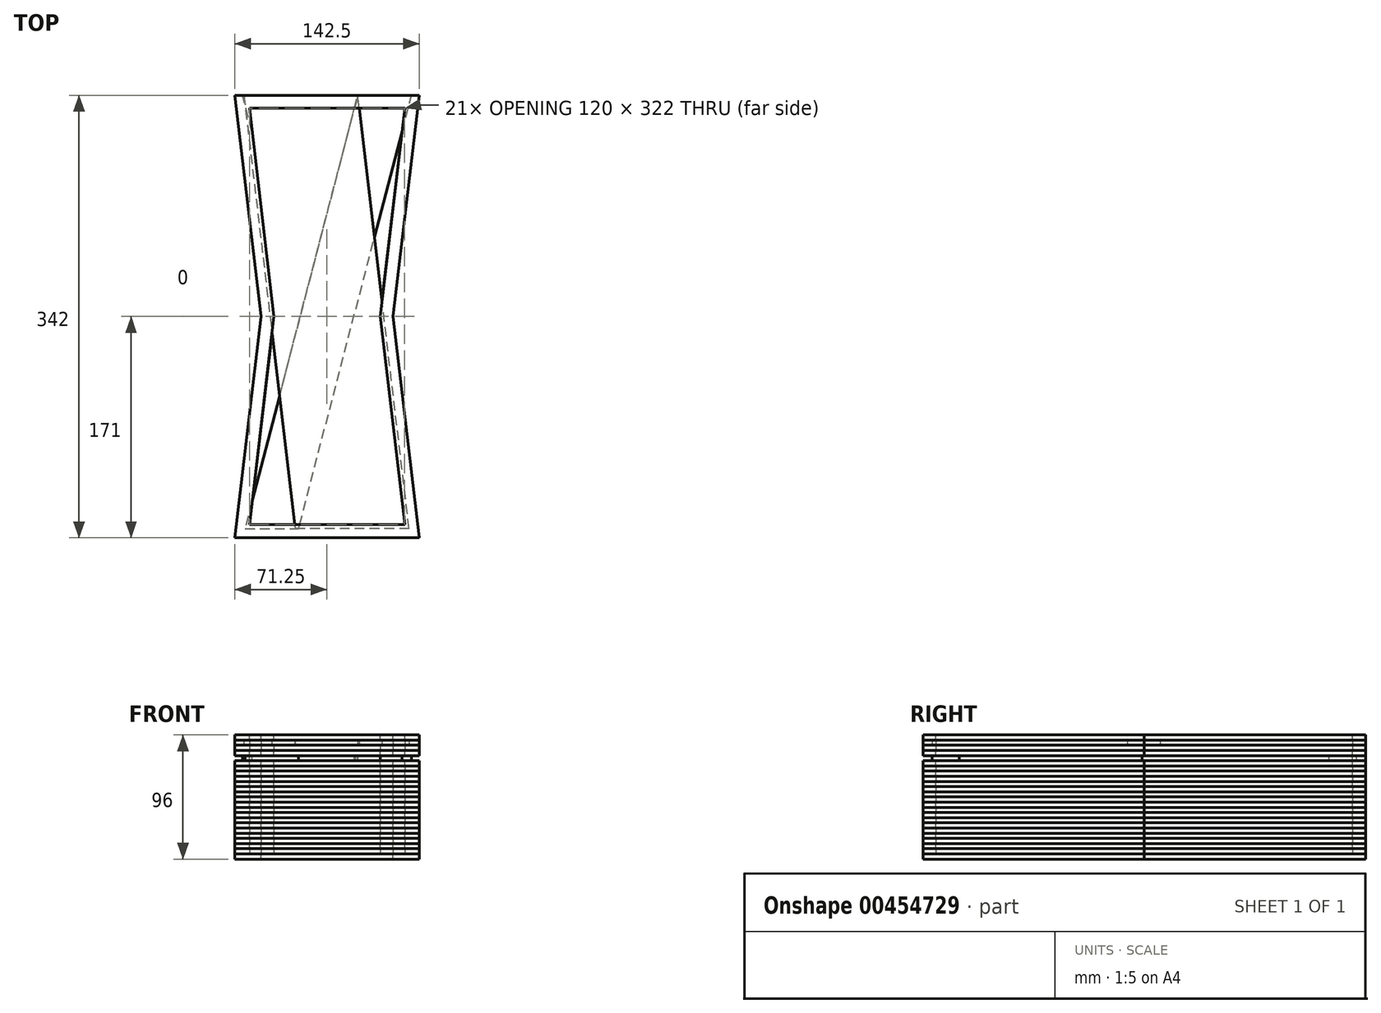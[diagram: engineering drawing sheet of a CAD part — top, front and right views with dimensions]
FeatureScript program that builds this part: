
annotation { "Feature Type Name" : "Feature", "Feature Type Description" : "" }
export const myFeature = defineFeature(function(context is Context, id is Id, definition is map)
    precondition{}
    {
        {
            var Q0;
            Q0=qCreatedBy(makeId("Top.planeOp"),FACE);
            var sketch = newSketch(context, id + "F0", { "sketchPlane" : qUnion([Q0])});
            skLineSegment(sketch, "E0", {"start": v(-71.25, -171) * mm, "end": v(-51.07, 0) * mm});
            skLineSegment(sketch, "E1", {"start": v(-51.07, 0) * mm, "end": v(-71.25, 171) * mm});
            skLineSegment(sketch, "E2", {"start": v(-71.25, 171) * mm, "end": v(71.25, 171) * mm});
            skLineSegment(sketch, "E3", {"start": v(71.25, 171) * mm, "end": v(51.07, 0) * mm});
            skLineSegment(sketch, "E4", {"start": v(51.07, 0) * mm, "end": v(71.25, -171) * mm});
            skLineSegment(sketch, "E5", {"start": v(71.25, -171) * mm, "end": v(-71.25, -171) * mm});
            skLineSegment(sketch, "E6", {"start": v(-60, -161) * mm, "end": v(-41, 0) * mm});
            skLineSegment(sketch, "E7", {"start": v(-41, 0) * mm, "end": v(-60, 161) * mm});
            skLineSegment(sketch, "E8", {"start": v(-60, 161) * mm, "end": v(60, 161) * mm});
            skLineSegment(sketch, "E9", {"start": v(60, 161) * mm, "end": v(41, 0) * mm});
            skLineSegment(sketch, "E10", {"start": v(41, 0) * mm, "end": v(60, -161) * mm});
            skLineSegment(sketch, "E11", {"start": v(60, -161) * mm, "end": v(-60, -161) * mm});
            skSolve(sketch);
        }
        {
            var Q0;
            Q0 = qSketchRegion(id + "F0", true);
            extrude(context, id + "F1", {"entities" : qUnion([Q0]), "depth" : 4 * mm});
        }
        {
            var Q0;
            Q0=makeQuery(id+"F1.opExtrude","CAP_FACE",FACE,{"disambiguationData":[OSD([sQuery(id+"F0.wireOp",EDGE,"E0"),sQuery(id+"F0.wireOp",EDGE,"E1"),sQuery(id+"F0.wireOp",EDGE,"E2"),sQuery(id+"F0.wireOp",EDGE,"E3"),sQuery(id+"F0.wireOp",EDGE,"E4"),sQuery(id+"F0.wireOp",EDGE,"E5"),sQuery(id+"F0.wireOp",EDGE,"E6"),sQuery(id+"F0.wireOp",EDGE,"E7"),sQuery(id+"F0.wireOp",EDGE,"E8"),sQuery(id+"F0.wireOp",EDGE,"E9"),sQuery(id+"F0.wireOp",EDGE,"E10"),sQuery(id+"F0.wireOp",EDGE,"E11")])],"isStart":false});
            var sketch = newSketch(context, id + "F2", { "sketchPlane" : qUnion([Q0])});
            skLineSegment(sketch, "E12", {"start": v(-71.25, -171) * mm, "end": v(-51.07, 0) * mm});
            skLineSegment(sketch, "E13", {"start": v(-51.07, 0) * mm, "end": v(-71.25, 171) * mm});
            skLineSegment(sketch, "E14", {"start": v(-71.25, 171) * mm, "end": v(-64.2, 171) * mm});
            skLineSegment(sketch, "E15", {"start": v(71.25, 171) * mm, "end": v(51.07, 0) * mm});
            skLineSegment(sketch, "E16", {"start": v(51.07, 0) * mm, "end": v(71.25, -171) * mm});
            skLineSegment(sketch, "E17", {"start": v(71.25, -171) * mm, "end": v(-71.25, -171) * mm});
            skLineSegment(sketch, "E18", {"start": v(63.38, -164) * mm, "end": v(42.46, 12.4) * mm});
            skLineSegment(sketch, "E19", {"start": v(42.46, 12.4) * mm, "end": v(60, 161) * mm});
            skLineSegment(sketch, "E20", {"start": v(60, 161) * mm, "end": v(24.84, 161) * mm});
            skLineSegment(sketch, "E21", {"start": v(24.84, 161) * mm, "end": v(24.49, 164) * mm});
            skLineSegment(sketch, "E22", {"start": v(-63.37, 164) * mm, "end": v(-42.52, -12.89) * mm});
            skLineSegment(sketch, "E23", {"start": v(-42.52, -12.89) * mm, "end": v(-60, -161) * mm});
            skLineSegment(sketch, "E24", {"start": v(-60, -161) * mm, "end": v(-25.06, -161) * mm});
            skLineSegment(sketch, "E25", {"start": v(-25.06, -161) * mm, "end": v(-24.7, -164) * mm});
            skLineSegment(sketch, "E26", {"start": v(63.38, -164) * mm, "end": v(-24.7, -164) * mm});
            skLineSegment(sketch, "E27", {"start": v(-63.37, 164) * mm, "end": v(-64.2, 171) * mm});
            skLineSegment(sketch, "E28", {"start": v(24.49, 164) * mm, "end": v(23.66, 171) * mm});
            skLineSegment(sketch, "E29.trimOffspring", {"start": v(23.66, 171) * mm, "end": v(71.25, 171) * mm});
            skSolve(sketch);
        }
        {
            var Q0;
            Q0 = qSketchRegion(id + "F2", true);
            extrude(context, id + "F3", {"entities" : qUnion([Q0]), "depth" : 4 * mm});
        }
        {
            var Q0;
            Q0=makeQuery(id+"F1.opExtrude","CAP_FACE",FACE,{"disambiguationData":[OSD([sQuery(id+"F0.wireOp",EDGE,"E0"),sQuery(id+"F0.wireOp",EDGE,"E1"),sQuery(id+"F0.wireOp",EDGE,"E2"),sQuery(id+"F0.wireOp",EDGE,"E3"),sQuery(id+"F0.wireOp",EDGE,"E4"),sQuery(id+"F0.wireOp",EDGE,"E5"),sQuery(id+"F0.wireOp",EDGE,"E6"),sQuery(id+"F0.wireOp",EDGE,"E7"),sQuery(id+"F0.wireOp",EDGE,"E8"),sQuery(id+"F0.wireOp",EDGE,"E9"),sQuery(id+"F0.wireOp",EDGE,"E10"),sQuery(id+"F0.wireOp",EDGE,"E11")])],"isStart":false});
            var Q1;
            Q1=makeQuery(id+"F3.opExtrude","CAP_FACE",FACE,{"disambiguationData":[OSD([sQuery(id+"F2.wireOp",EDGE,"E12"),sQuery(id+"F2.wireOp",EDGE,"E13"),sQuery(id+"F2.wireOp",EDGE,"E14"),sQuery(id+"F2.wireOp",EDGE,"E15"),sQuery(id+"F2.wireOp",EDGE,"E16"),sQuery(id+"F2.wireOp",EDGE,"E17"),sQuery(id+"F2.wireOp",EDGE,"E18"),sQuery(id+"F2.wireOp",EDGE,"E19"),sQuery(id+"F2.wireOp",EDGE,"E20"),sQuery(id+"F2.wireOp",EDGE,"E21"),sQuery(id+"F2.wireOp",EDGE,"E22"),sQuery(id+"F2.wireOp",EDGE,"E23"),sQuery(id+"F2.wireOp",EDGE,"E24"),sQuery(id+"F2.wireOp",EDGE,"E25"),sQuery(id+"F2.wireOp",EDGE,"E26"),sQuery(id+"F2.wireOp",EDGE,"E27"),sQuery(id+"F2.wireOp",EDGE,"E28"),sQuery(id+"F2.wireOp",EDGE,"E29.trimOffspring")])],"isStart":false});
            cPlane(context, id + "F4", {"entities" : qUnion([Q0, Q1]), "cplaneType" : CPlaneType.MID_PLANE, "offset" : 25 * mm, "width" : 150 * mm, "height" : 150 * mm});
        }
        {
            var Q0;
            Q0=makeQuery(id+"F1.opExtrude","SWEPT_BODY",BODY,{"disambiguationData":[OSD([sQuery(id+"F0.wireOp",EDGE,"E0"),sQuery(id+"F0.wireOp",EDGE,"E1"),sQuery(id+"F0.wireOp",EDGE,"E2"),sQuery(id+"F0.wireOp",EDGE,"E3"),sQuery(id+"F0.wireOp",EDGE,"E4"),sQuery(id+"F0.wireOp",EDGE,"E5"),sQuery(id+"F0.wireOp",EDGE,"E6"),sQuery(id+"F0.wireOp",EDGE,"E7"),sQuery(id+"F0.wireOp",EDGE,"E8"),sQuery(id+"F0.wireOp",EDGE,"E9"),sQuery(id+"F0.wireOp",EDGE,"E10"),sQuery(id+"F0.wireOp",EDGE,"E11")])]});
            var Q1;
            Q1=qCreatedBy(id+"F4.planeOp",FACE);
            mirror(context, id + "F5", {"entities" : qUnion([Q0]), "mirrorPlane" : qUnion([Q1])});
        }
        {
            var Q0;
            Q0=makeQuery(id+"F1.opExtrude","CAP_FACE",FACE,{"disambiguationData":[OSD([sQuery(id+"F0.wireOp",EDGE,"E0"),sQuery(id+"F0.wireOp",EDGE,"E1"),sQuery(id+"F0.wireOp",EDGE,"E2"),sQuery(id+"F0.wireOp",EDGE,"E3"),sQuery(id+"F0.wireOp",EDGE,"E4"),sQuery(id+"F0.wireOp",EDGE,"E5"),sQuery(id+"F0.wireOp",EDGE,"E6"),sQuery(id+"F0.wireOp",EDGE,"E7"),sQuery(id+"F0.wireOp",EDGE,"E8"),sQuery(id+"F0.wireOp",EDGE,"E9"),sQuery(id+"F0.wireOp",EDGE,"E10"),sQuery(id+"F0.wireOp",EDGE,"E11")])],"isStart":false});
            var sketch = newSketch(context, id + "F6", { "sketchPlane" : qUnion([Q0])});
            skLineSegment(sketch, "E30", {"start": v(-64.24, 171) * mm, "end": v(-24.7, -164) * mm});
            skLineSegment(sketch, "E31", {"start": v(23.66, 171) * mm, "end": v(-64.24, 171) * mm});
            skLineSegment(sketch, "E32", {"start": v(-24.7, -164) * mm, "end": v(63.38, -164) * mm});
            skLineSegment(sketch, "E33", {"start": v(63.38, -164) * mm, "end": v(23.66, 171) * mm});
            skSolve(sketch);
        }
        {
            var Q0;
            Q0 = qSketchRegion(id + "F6", true);
            extrude(context, id + "F7", {"entities" : qUnion([Q0]), "depth" : 4 * mm});
        }
        {
            var Q0;
            Q0=makeQuery(id+"F1.opExtrude","SWEPT_BODY",BODY,{"disambiguationData":[OSD([sQuery(id+"F0.wireOp",EDGE,"E0"),sQuery(id+"F0.wireOp",EDGE,"E1"),sQuery(id+"F0.wireOp",EDGE,"E2"),sQuery(id+"F0.wireOp",EDGE,"E3"),sQuery(id+"F0.wireOp",EDGE,"E4"),sQuery(id+"F0.wireOp",EDGE,"E5"),sQuery(id+"F0.wireOp",EDGE,"E6"),sQuery(id+"F0.wireOp",EDGE,"E7"),sQuery(id+"F0.wireOp",EDGE,"E8"),sQuery(id+"F0.wireOp",EDGE,"E9"),sQuery(id+"F0.wireOp",EDGE,"E10"),sQuery(id+"F0.wireOp",EDGE,"E11")])]});
            var Q1;
            Q1=makeQuery(id+"F1.opExtrude","CAP_FACE",FACE,{"disambiguationData":[OSD([sQuery(id+"F0.wireOp",EDGE,"E0"),sQuery(id+"F0.wireOp",EDGE,"E1"),sQuery(id+"F0.wireOp",EDGE,"E2"),sQuery(id+"F0.wireOp",EDGE,"E3"),sQuery(id+"F0.wireOp",EDGE,"E4"),sQuery(id+"F0.wireOp",EDGE,"E5"),sQuery(id+"F0.wireOp",EDGE,"E6"),sQuery(id+"F0.wireOp",EDGE,"E7"),sQuery(id+"F0.wireOp",EDGE,"E8"),sQuery(id+"F0.wireOp",EDGE,"E9"),sQuery(id+"F0.wireOp",EDGE,"E10"),sQuery(id+"F0.wireOp",EDGE,"E11")])],"isStart":true});
            mirror(context, id + "F8", {"entities" : qUnion([Q0]), "mirrorPlane" : qUnion([Q1])});
        }
        {
            var Q0;
            Q0=makeQuery(id+"F8.opPattern","COPY",FACE,{"derivedFrom":makeQuery(id+"F1.opExtrude","CAP_FACE",FACE,{"disambiguationData":[OSD([sQuery(id+"F0.wireOp",EDGE,"E0"),sQuery(id+"F0.wireOp",EDGE,"E1"),sQuery(id+"F0.wireOp",EDGE,"E2"),sQuery(id+"F0.wireOp",EDGE,"E3"),sQuery(id+"F0.wireOp",EDGE,"E4"),sQuery(id+"F0.wireOp",EDGE,"E5"),sQuery(id+"F0.wireOp",EDGE,"E6"),sQuery(id+"F0.wireOp",EDGE,"E7"),sQuery(id+"F0.wireOp",EDGE,"E8"),sQuery(id+"F0.wireOp",EDGE,"E9"),sQuery(id+"F0.wireOp",EDGE,"E10"),sQuery(id+"F0.wireOp",EDGE,"E11")])],"isStart":false}),"instanceName":"1"});
            var sketch = newSketch(context, id + "F9", { "sketchPlane" : qUnion([Q0])});
            skLineSegment(sketch, "E34", {"start": v(-71.25, -171) * mm, "end": v(-51.07, 0) * mm});
            skLineSegment(sketch, "E35", {"start": v(-51.07, 0) * mm, "end": v(-71.25, 171) * mm});
            skLineSegment(sketch, "E36", {"start": v(-71.25, 171) * mm, "end": v(71.25, 171) * mm});
            skLineSegment(sketch, "E37", {"start": v(71.25, 171) * mm, "end": v(51.07, 0) * mm});
            skLineSegment(sketch, "E38", {"start": v(51.07, 0) * mm, "end": v(71.25, -171) * mm});
            skLineSegment(sketch, "E39", {"start": v(71.25, -171) * mm, "end": v(-23.82, -171) * mm});
            skLineSegment(sketch, "E40", {"start": v(41, 0) * mm, "end": v(57.89, 143.12) * mm});
            skLineSegment(sketch, "E41", {"start": v(57.89, 143.12) * mm, "end": v(63.32, 164) * mm});
            skLineSegment(sketch, "E42", {"start": v(63.32, 164) * mm, "end": v(21.96, 164) * mm});
            skLineSegment(sketch, "E43", {"start": v(21.96, 164) * mm, "end": v(21.18, 161) * mm});
            skLineSegment(sketch, "E44", {"start": v(21.18, 161) * mm, "end": v(-60, 161) * mm});
            skLineSegment(sketch, "E45", {"start": v(-60, 161) * mm, "end": v(-41, 0) * mm});
            skLineSegment(sketch, "E46", {"start": v(-41, 0) * mm, "end": v(-57.85, -142.75) * mm});
            skLineSegment(sketch, "E47", {"start": v(-57.85, -142.75) * mm, "end": v(-63.37, -164) * mm});
            skLineSegment(sketch, "E48", {"start": v(-22, -164) * mm, "end": v(-21.22, -161) * mm});
            skLineSegment(sketch, "E49", {"start": v(-21.22, -161) * mm, "end": v(60, -161) * mm});
            skLineSegment(sketch, "E50", {"start": v(60, -161) * mm, "end": v(41, 0) * mm});
            skLineSegment(sketch, "E51", {"start": v(-63.37, -164) * mm, "end": v(-65.2, -171) * mm});
            skLineSegment(sketch, "E52", {"start": v(-22, -164) * mm, "end": v(-23.82, -171) * mm});
            skLineSegment(sketch, "E53.trimOffspring", {"start": v(-65.2, -171) * mm, "end": v(-71.25, -171) * mm});
            skLineSegment(sketch, "E54", {"start": v(0, 0) * mm, "end": v(0, -54.2) * mm, "construction": true});
            skLineSegment(sketch, "E55.MirrorCS", {"start": v(22, -164) * mm, "end": v(21.22, -161) * mm});
            skLineSegment(sketch, "E56.MirrorCS", {"start": v(22, -164) * mm, "end": v(23.82, -171) * mm});
            skLineSegment(sketch, "E57.MirrorCS", {"start": v(65.2, -171) * mm, "end": v(71.25, -171) * mm});
            skLineSegment(sketch, "E58.MirrorCS", {"start": v(63.37, -164) * mm, "end": v(65.2, -171) * mm});
            skLineSegment(sketch, "E59.MirrorCS", {"start": v(-21.96, 164) * mm, "end": v(-21.18, 161) * mm});
            skLineSegment(sketch, "E60.MirrorCS", {"start": v(51.07, 0) * mm, "end": v(71.25, 171) * mm});
            skLineSegment(sketch, "E61.MirrorCS", {"start": v(21.22, -161) * mm, "end": v(-60, -161) * mm});
            skLineSegment(sketch, "E62.MirrorCS", {"start": v(-57.89, 143.12) * mm, "end": v(-63.32, 164) * mm});
            skLineSegment(sketch, "E63.MirrorCS", {"start": v(71.25, -171) * mm, "end": v(51.07, 0) * mm});
            skLineSegment(sketch, "E64.MirrorCS", {"start": v(-60, -161) * mm, "end": v(-41, 0) * mm});
            skLineSegment(sketch, "E65.MirrorCS", {"start": v(71.25, 171) * mm, "end": v(-71.25, 171) * mm});
            skLineSegment(sketch, "E66.MirrorCS", {"start": v(60, 161) * mm, "end": v(41, 0) * mm});
            skLineSegment(sketch, "E67.MirrorCS", {"start": v(-63.32, 164) * mm, "end": v(-21.96, 164) * mm});
            skLineSegment(sketch, "E68.MirrorCS", {"start": v(57.85, -142.75) * mm, "end": v(63.37, -164) * mm});
            skLineSegment(sketch, "E69.MirrorCS", {"start": v(41, 0) * mm, "end": v(57.85, -142.75) * mm});
            skLineSegment(sketch, "E70.MirrorCS", {"start": v(-21.18, 161) * mm, "end": v(60, 161) * mm});
            skLineSegment(sketch, "E71.MirrorCS", {"start": v(-71.25, -171) * mm, "end": v(23.82, -171) * mm});
            skLineSegment(sketch, "E72.MirrorCS", {"start": v(-41, 0) * mm, "end": v(-57.89, 143.12) * mm});
            skLineSegment(sketch, "E73.MirrorCS", {"start": v(-71.25, 171) * mm, "end": v(-51.07, 0) * mm});
            skLineSegment(sketch, "E74.MirrorCS", {"start": v(-51.07, 0) * mm, "end": v(-71.25, -171) * mm});
            skSolve(sketch);
        }
        {
            var Q0;
            {var subQ8=sQuery(id+"F9.wireOp",EDGE,"E41");Q0=makeQuery(id+"F9.imprint","IMPRINT",FACE,{"disambiguationData":[TD([[makeQuery(id+"F9.imprint","IMPRINT",EDGE,{"derivedFrom":subQ8}),-1.0]])]});}
            var sketch = newSketch(context, id + "F10", { "sketchPlane" : qUnion([Q0])});
            skLineSegment(sketch, "E75", {"start": v(71.25, -171) * mm, "end": v(51.07, 0) * mm});
            skLineSegment(sketch, "E76", {"start": v(51.07, 0) * mm, "end": v(71.25, 171) * mm});
            skLineSegment(sketch, "E77", {"start": v(71.25, 171) * mm, "end": v(-71.25, 171) * mm});
            skLineSegment(sketch, "E78", {"start": v(-71.25, 171) * mm, "end": v(-51.07, 0) * mm});
            skLineSegment(sketch, "E79", {"start": v(-51.07, 0) * mm, "end": v(-71.25, -171) * mm});
            skLineSegment(sketch, "E80", {"start": v(-71.25, -171) * mm, "end": v(71.25, -171) * mm});
            skLineSegment(sketch, "E81", {"start": v(-41, 0) * mm, "end": v(-57.89, 143.12) * mm});
            skLineSegment(sketch, "E82", {"start": v(-57.89, 143.12) * mm, "end": v(-63.32, 164) * mm});
            skLineSegment(sketch, "E83", {"start": v(-63.32, 164) * mm, "end": v(-21.96, 164) * mm});
            skLineSegment(sketch, "E84", {"start": v(-21.96, 164) * mm, "end": v(-21.18, 161) * mm});
            skLineSegment(sketch, "E85", {"start": v(-21.18, 161) * mm, "end": v(60, 161) * mm});
            skLineSegment(sketch, "E86", {"start": v(60, 161) * mm, "end": v(41, 0) * mm});
            skLineSegment(sketch, "E87", {"start": v(41, 0) * mm, "end": v(57.85, -142.75) * mm});
            skLineSegment(sketch, "E88", {"start": v(57.85, -142.75) * mm, "end": v(63.37, -164) * mm});
            skLineSegment(sketch, "E89", {"start": v(22, -164) * mm, "end": v(21.22, -161) * mm});
            skLineSegment(sketch, "E90", {"start": v(21.22, -161) * mm, "end": v(-60, -161) * mm});
            skLineSegment(sketch, "E91", {"start": v(-60, -161) * mm, "end": v(-41, 0) * mm});
            skLineSegment(sketch, "E92", {"start": v(-57.89, 143.12) * mm, "end": v(21.22, -161) * mm});
            skLineSegment(sketch, "E93", {"start": v(-21.18, 161) * mm, "end": v(57.85, -142.75) * mm});
            skLineSegment(sketch, "E94", {"start": v(63.37, -164) * mm, "end": v(65.2, -171) * mm});
            skLineSegment(sketch, "E95", {"start": v(65.2, -171) * mm, "end": v(24.02, -171) * mm});
            skLineSegment(sketch, "E96", {"start": v(24.02, -171) * mm, "end": v(22, -164) * mm});
            skSolve(sketch);
        }
        {
            var Q0;
            {var subQ2=sQuery(id+"F10.wireOp",EDGE,"E83");Q0=makeQuery(id+"F10.imprint","IMPRINT",FACE,{"disambiguationData":[TD([[makeQuery(id+"F10.imprint","IMPRINT",EDGE,{"derivedFrom":subQ2}),-1.0]])]});}
            extrude(context, id + "F11", {"entities" : qUnion([Q0]), "depth" : 4 * mm});
        }
        {
            var Q0;
            {var subQ3=sQuery(id+"F9.wireOp",EDGE,"E48");Q0=makeQuery(id+"F9.imprint","IMPRINT",FACE,{"disambiguationData":[TD([[makeQuery(id+"F9.imprint","IMPRINT",EDGE,{"derivedFrom":subQ3}),-1.0]])]});}
            var Q1;
            {var subQ1=sQuery(id+"F9.wireOp",EDGE,"E48");Q1=makeQuery(id+"F9.imprint","IMPRINT",FACE,{"disambiguationData":[TD([[makeQuery(id+"F9.imprint","IMPRINT",EDGE,{"derivedFrom":subQ1}),1.0]])]});}
            var Q2;
            {var subQ8=sQuery(id+"F9.wireOp",EDGE,"E41");Q2=makeQuery(id+"F9.imprint","IMPRINT",FACE,{"disambiguationData":[TD([[makeQuery(id+"F9.imprint","IMPRINT",EDGE,{"derivedFrom":subQ8}),-1.0]])]});}
            extrude(context, id + "F12", {"entities" : qUnion([Q0, Q1, Q2]), "depth" : 4 * mm});
        }
        {
            var Q0;
            Q0=makeQuery(id+"F1.opExtrude","SWEPT_BODY",BODY,{"disambiguationData":[OSD([sQuery(id+"F0.wireOp",EDGE,"E0"),sQuery(id+"F0.wireOp",EDGE,"E1"),sQuery(id+"F0.wireOp",EDGE,"E2"),sQuery(id+"F0.wireOp",EDGE,"E3"),sQuery(id+"F0.wireOp",EDGE,"E4"),sQuery(id+"F0.wireOp",EDGE,"E5"),sQuery(id+"F0.wireOp",EDGE,"E6"),sQuery(id+"F0.wireOp",EDGE,"E7"),sQuery(id+"F0.wireOp",EDGE,"E8"),sQuery(id+"F0.wireOp",EDGE,"E9"),sQuery(id+"F0.wireOp",EDGE,"E10"),sQuery(id+"F0.wireOp",EDGE,"E11")])]});
            var Q1;
            Q1=makeQuery(id+"F8.opPattern","COPY",FACE,{"derivedFrom":makeQuery(id+"F1.opExtrude","CAP_FACE",FACE,{"disambiguationData":[OSD([sQuery(id+"F0.wireOp",EDGE,"E0"),sQuery(id+"F0.wireOp",EDGE,"E1"),sQuery(id+"F0.wireOp",EDGE,"E2"),sQuery(id+"F0.wireOp",EDGE,"E3"),sQuery(id+"F0.wireOp",EDGE,"E4"),sQuery(id+"F0.wireOp",EDGE,"E5"),sQuery(id+"F0.wireOp",EDGE,"E6"),sQuery(id+"F0.wireOp",EDGE,"E7"),sQuery(id+"F0.wireOp",EDGE,"E8"),sQuery(id+"F0.wireOp",EDGE,"E9"),sQuery(id+"F0.wireOp",EDGE,"E10"),sQuery(id+"F0.wireOp",EDGE,"E11")])],"isStart":false}),"instanceName":"1"});
            mirror(context, id + "F13", {"entities" : qUnion([Q0]), "mirrorPlane" : qUnion([Q1])});
        }
        {
            var Q0;
            Q0=makeQuery(id+"F13.opPattern","COPY",BODY,{"derivedFrom":makeQuery(id+"F1.opExtrude","SWEPT_BODY",BODY,{"disambiguationData":[OSD([sQuery(id+"F0.wireOp",EDGE,"E0"),sQuery(id+"F0.wireOp",EDGE,"E1"),sQuery(id+"F0.wireOp",EDGE,"E2"),sQuery(id+"F0.wireOp",EDGE,"E3"),sQuery(id+"F0.wireOp",EDGE,"E4"),sQuery(id+"F0.wireOp",EDGE,"E5"),sQuery(id+"F0.wireOp",EDGE,"E6"),sQuery(id+"F0.wireOp",EDGE,"E7"),sQuery(id+"F0.wireOp",EDGE,"E8"),sQuery(id+"F0.wireOp",EDGE,"E9"),sQuery(id+"F0.wireOp",EDGE,"E10"),sQuery(id+"F0.wireOp",EDGE,"E11")])]}),"instanceName":"1"});
            var Q1;
            Q1=makeQuery(id+"F13.opPattern","COPY",FACE,{"derivedFrom":makeQuery(id+"F1.opExtrude","CAP_FACE",FACE,{"disambiguationData":[OSD([sQuery(id+"F0.wireOp",EDGE,"E0"),sQuery(id+"F0.wireOp",EDGE,"E1"),sQuery(id+"F0.wireOp",EDGE,"E2"),sQuery(id+"F0.wireOp",EDGE,"E3"),sQuery(id+"F0.wireOp",EDGE,"E4"),sQuery(id+"F0.wireOp",EDGE,"E5"),sQuery(id+"F0.wireOp",EDGE,"E6"),sQuery(id+"F0.wireOp",EDGE,"E7"),sQuery(id+"F0.wireOp",EDGE,"E8"),sQuery(id+"F0.wireOp",EDGE,"E9"),sQuery(id+"F0.wireOp",EDGE,"E10"),sQuery(id+"F0.wireOp",EDGE,"E11")])],"isStart":false}),"instanceName":"1"});
            mirror(context, id + "F14", {"entities" : qUnion([Q0]), "mirrorPlane" : qUnion([Q1])});
        }
        {
            var Q0;
            Q0=makeQuery(id+"F14.opPattern","COPY",BODY,{"derivedFrom":makeQuery(id+"F13.opPattern","COPY",BODY,{"derivedFrom":makeQuery(id+"F1.opExtrude","SWEPT_BODY",BODY,{"disambiguationData":[OSD([sQuery(id+"F0.wireOp",EDGE,"E0"),sQuery(id+"F0.wireOp",EDGE,"E1"),sQuery(id+"F0.wireOp",EDGE,"E2"),sQuery(id+"F0.wireOp",EDGE,"E3"),sQuery(id+"F0.wireOp",EDGE,"E4"),sQuery(id+"F0.wireOp",EDGE,"E5"),sQuery(id+"F0.wireOp",EDGE,"E6"),sQuery(id+"F0.wireOp",EDGE,"E7"),sQuery(id+"F0.wireOp",EDGE,"E8"),sQuery(id+"F0.wireOp",EDGE,"E9"),sQuery(id+"F0.wireOp",EDGE,"E10"),sQuery(id+"F0.wireOp",EDGE,"E11")])]}),"instanceName":"1"}),"instanceName":"1"});
            var Q1;
            Q1=makeQuery(id+"F13.opPattern","COPY",BODY,{"derivedFrom":makeQuery(id+"F1.opExtrude","SWEPT_BODY",BODY,{"disambiguationData":[OSD([sQuery(id+"F0.wireOp",EDGE,"E0"),sQuery(id+"F0.wireOp",EDGE,"E1"),sQuery(id+"F0.wireOp",EDGE,"E2"),sQuery(id+"F0.wireOp",EDGE,"E3"),sQuery(id+"F0.wireOp",EDGE,"E4"),sQuery(id+"F0.wireOp",EDGE,"E5"),sQuery(id+"F0.wireOp",EDGE,"E6"),sQuery(id+"F0.wireOp",EDGE,"E7"),sQuery(id+"F0.wireOp",EDGE,"E8"),sQuery(id+"F0.wireOp",EDGE,"E9"),sQuery(id+"F0.wireOp",EDGE,"E10"),sQuery(id+"F0.wireOp",EDGE,"E11")])]}),"instanceName":"1"});
            var Q2;
            Q2=makeQuery(id+"F14.opPattern","COPY",FACE,{"derivedFrom":makeQuery(id+"F13.opPattern","COPY",FACE,{"derivedFrom":makeQuery(id+"F1.opExtrude","CAP_FACE",FACE,{"disambiguationData":[OSD([sQuery(id+"F0.wireOp",EDGE,"E0"),sQuery(id+"F0.wireOp",EDGE,"E1"),sQuery(id+"F0.wireOp",EDGE,"E2"),sQuery(id+"F0.wireOp",EDGE,"E3"),sQuery(id+"F0.wireOp",EDGE,"E4"),sQuery(id+"F0.wireOp",EDGE,"E5"),sQuery(id+"F0.wireOp",EDGE,"E6"),sQuery(id+"F0.wireOp",EDGE,"E7"),sQuery(id+"F0.wireOp",EDGE,"E8"),sQuery(id+"F0.wireOp",EDGE,"E9"),sQuery(id+"F0.wireOp",EDGE,"E10"),sQuery(id+"F0.wireOp",EDGE,"E11")])],"isStart":true}),"instanceName":"1"}),"instanceName":"1"});
            mirror(context, id + "F15", {"entities" : qUnion([Q0, Q1]), "mirrorPlane" : qUnion([Q2])});
        }
        {
            var Q0;
            Q0=makeQuery(id+"F15.opPattern","COPY",BODY,{"derivedFrom":makeQuery(id+"F13.opPattern","COPY",BODY,{"derivedFrom":makeQuery(id+"F1.opExtrude","SWEPT_BODY",BODY,{"disambiguationData":[OSD([sQuery(id+"F0.wireOp",EDGE,"E0"),sQuery(id+"F0.wireOp",EDGE,"E1"),sQuery(id+"F0.wireOp",EDGE,"E2"),sQuery(id+"F0.wireOp",EDGE,"E3"),sQuery(id+"F0.wireOp",EDGE,"E4"),sQuery(id+"F0.wireOp",EDGE,"E5"),sQuery(id+"F0.wireOp",EDGE,"E6"),sQuery(id+"F0.wireOp",EDGE,"E7"),sQuery(id+"F0.wireOp",EDGE,"E8"),sQuery(id+"F0.wireOp",EDGE,"E9"),sQuery(id+"F0.wireOp",EDGE,"E10"),sQuery(id+"F0.wireOp",EDGE,"E11")])]}),"instanceName":"1"}),"instanceName":"1"});
            var Q1;
            Q1=makeQuery(id+"F15.opPattern","COPY",BODY,{"derivedFrom":makeQuery(id+"F14.opPattern","COPY",BODY,{"derivedFrom":makeQuery(id+"F13.opPattern","COPY",BODY,{"derivedFrom":makeQuery(id+"F1.opExtrude","SWEPT_BODY",BODY,{"disambiguationData":[OSD([sQuery(id+"F0.wireOp",EDGE,"E0"),sQuery(id+"F0.wireOp",EDGE,"E1"),sQuery(id+"F0.wireOp",EDGE,"E2"),sQuery(id+"F0.wireOp",EDGE,"E3"),sQuery(id+"F0.wireOp",EDGE,"E4"),sQuery(id+"F0.wireOp",EDGE,"E5"),sQuery(id+"F0.wireOp",EDGE,"E6"),sQuery(id+"F0.wireOp",EDGE,"E7"),sQuery(id+"F0.wireOp",EDGE,"E8"),sQuery(id+"F0.wireOp",EDGE,"E9"),sQuery(id+"F0.wireOp",EDGE,"E10"),sQuery(id+"F0.wireOp",EDGE,"E11")])]}),"instanceName":"1"}),"instanceName":"1"}),"instanceName":"1"});
            var Q2;
            Q2=makeQuery(id+"F14.opPattern","COPY",BODY,{"derivedFrom":makeQuery(id+"F13.opPattern","COPY",BODY,{"derivedFrom":makeQuery(id+"F1.opExtrude","SWEPT_BODY",BODY,{"disambiguationData":[OSD([sQuery(id+"F0.wireOp",EDGE,"E0"),sQuery(id+"F0.wireOp",EDGE,"E1"),sQuery(id+"F0.wireOp",EDGE,"E2"),sQuery(id+"F0.wireOp",EDGE,"E3"),sQuery(id+"F0.wireOp",EDGE,"E4"),sQuery(id+"F0.wireOp",EDGE,"E5"),sQuery(id+"F0.wireOp",EDGE,"E6"),sQuery(id+"F0.wireOp",EDGE,"E7"),sQuery(id+"F0.wireOp",EDGE,"E8"),sQuery(id+"F0.wireOp",EDGE,"E9"),sQuery(id+"F0.wireOp",EDGE,"E10"),sQuery(id+"F0.wireOp",EDGE,"E11")])]}),"instanceName":"1"}),"instanceName":"1"});
            var Q3;
            Q3=makeQuery(id+"F13.opPattern","COPY",BODY,{"derivedFrom":makeQuery(id+"F1.opExtrude","SWEPT_BODY",BODY,{"disambiguationData":[OSD([sQuery(id+"F0.wireOp",EDGE,"E0"),sQuery(id+"F0.wireOp",EDGE,"E1"),sQuery(id+"F0.wireOp",EDGE,"E2"),sQuery(id+"F0.wireOp",EDGE,"E3"),sQuery(id+"F0.wireOp",EDGE,"E4"),sQuery(id+"F0.wireOp",EDGE,"E5"),sQuery(id+"F0.wireOp",EDGE,"E6"),sQuery(id+"F0.wireOp",EDGE,"E7"),sQuery(id+"F0.wireOp",EDGE,"E8"),sQuery(id+"F0.wireOp",EDGE,"E9"),sQuery(id+"F0.wireOp",EDGE,"E10"),sQuery(id+"F0.wireOp",EDGE,"E11")])]}),"instanceName":"1"});
            var Q4;
            Q4=makeQuery(id+"F15.opPattern","COPY",FACE,{"derivedFrom":makeQuery(id+"F13.opPattern","COPY",FACE,{"derivedFrom":makeQuery(id+"F1.opExtrude","CAP_FACE",FACE,{"disambiguationData":[OSD([sQuery(id+"F0.wireOp",EDGE,"E0"),sQuery(id+"F0.wireOp",EDGE,"E1"),sQuery(id+"F0.wireOp",EDGE,"E2"),sQuery(id+"F0.wireOp",EDGE,"E3"),sQuery(id+"F0.wireOp",EDGE,"E4"),sQuery(id+"F0.wireOp",EDGE,"E5"),sQuery(id+"F0.wireOp",EDGE,"E6"),sQuery(id+"F0.wireOp",EDGE,"E7"),sQuery(id+"F0.wireOp",EDGE,"E8"),sQuery(id+"F0.wireOp",EDGE,"E9"),sQuery(id+"F0.wireOp",EDGE,"E10"),sQuery(id+"F0.wireOp",EDGE,"E11")])],"isStart":true}),"instanceName":"1"}),"instanceName":"1"});
            mirror(context, id + "F16", {"entities" : qUnion([Q0, Q1, Q2, Q3]), "mirrorPlane" : qUnion([Q4])});
        }
        {
            var Q0;
            Q0=makeQuery(id+"F16.opPattern","COPY",BODY,{"derivedFrom":makeQuery(id+"F13.opPattern","COPY",BODY,{"derivedFrom":makeQuery(id+"F1.opExtrude","SWEPT_BODY",BODY,{"disambiguationData":[OSD([sQuery(id+"F0.wireOp",EDGE,"E0"),sQuery(id+"F0.wireOp",EDGE,"E1"),sQuery(id+"F0.wireOp",EDGE,"E2"),sQuery(id+"F0.wireOp",EDGE,"E3"),sQuery(id+"F0.wireOp",EDGE,"E4"),sQuery(id+"F0.wireOp",EDGE,"E5"),sQuery(id+"F0.wireOp",EDGE,"E6"),sQuery(id+"F0.wireOp",EDGE,"E7"),sQuery(id+"F0.wireOp",EDGE,"E8"),sQuery(id+"F0.wireOp",EDGE,"E9"),sQuery(id+"F0.wireOp",EDGE,"E10"),sQuery(id+"F0.wireOp",EDGE,"E11")])]}),"instanceName":"1"}),"instanceName":"1"});
            var Q1;
            Q1=makeQuery(id+"F16.opPattern","COPY",BODY,{"derivedFrom":makeQuery(id+"F14.opPattern","COPY",BODY,{"derivedFrom":makeQuery(id+"F13.opPattern","COPY",BODY,{"derivedFrom":makeQuery(id+"F1.opExtrude","SWEPT_BODY",BODY,{"disambiguationData":[OSD([sQuery(id+"F0.wireOp",EDGE,"E0"),sQuery(id+"F0.wireOp",EDGE,"E1"),sQuery(id+"F0.wireOp",EDGE,"E2"),sQuery(id+"F0.wireOp",EDGE,"E3"),sQuery(id+"F0.wireOp",EDGE,"E4"),sQuery(id+"F0.wireOp",EDGE,"E5"),sQuery(id+"F0.wireOp",EDGE,"E6"),sQuery(id+"F0.wireOp",EDGE,"E7"),sQuery(id+"F0.wireOp",EDGE,"E8"),sQuery(id+"F0.wireOp",EDGE,"E9"),sQuery(id+"F0.wireOp",EDGE,"E10"),sQuery(id+"F0.wireOp",EDGE,"E11")])]}),"instanceName":"1"}),"instanceName":"1"}),"instanceName":"1"});
            var Q2;
            Q2=makeQuery(id+"F16.opPattern","COPY",BODY,{"derivedFrom":makeQuery(id+"F15.opPattern","COPY",BODY,{"derivedFrom":makeQuery(id+"F14.opPattern","COPY",BODY,{"derivedFrom":makeQuery(id+"F13.opPattern","COPY",BODY,{"derivedFrom":makeQuery(id+"F1.opExtrude","SWEPT_BODY",BODY,{"disambiguationData":[OSD([sQuery(id+"F0.wireOp",EDGE,"E0"),sQuery(id+"F0.wireOp",EDGE,"E1"),sQuery(id+"F0.wireOp",EDGE,"E2"),sQuery(id+"F0.wireOp",EDGE,"E3"),sQuery(id+"F0.wireOp",EDGE,"E4"),sQuery(id+"F0.wireOp",EDGE,"E5"),sQuery(id+"F0.wireOp",EDGE,"E6"),sQuery(id+"F0.wireOp",EDGE,"E7"),sQuery(id+"F0.wireOp",EDGE,"E8"),sQuery(id+"F0.wireOp",EDGE,"E9"),sQuery(id+"F0.wireOp",EDGE,"E10"),sQuery(id+"F0.wireOp",EDGE,"E11")])]}),"instanceName":"1"}),"instanceName":"1"}),"instanceName":"1"}),"instanceName":"1"});
            var Q3;
            Q3=makeQuery(id+"F16.opPattern","COPY",BODY,{"derivedFrom":makeQuery(id+"F15.opPattern","COPY",BODY,{"derivedFrom":makeQuery(id+"F13.opPattern","COPY",BODY,{"derivedFrom":makeQuery(id+"F1.opExtrude","SWEPT_BODY",BODY,{"disambiguationData":[OSD([sQuery(id+"F0.wireOp",EDGE,"E0"),sQuery(id+"F0.wireOp",EDGE,"E1"),sQuery(id+"F0.wireOp",EDGE,"E2"),sQuery(id+"F0.wireOp",EDGE,"E3"),sQuery(id+"F0.wireOp",EDGE,"E4"),sQuery(id+"F0.wireOp",EDGE,"E5"),sQuery(id+"F0.wireOp",EDGE,"E6"),sQuery(id+"F0.wireOp",EDGE,"E7"),sQuery(id+"F0.wireOp",EDGE,"E8"),sQuery(id+"F0.wireOp",EDGE,"E9"),sQuery(id+"F0.wireOp",EDGE,"E10"),sQuery(id+"F0.wireOp",EDGE,"E11")])]}),"instanceName":"1"}),"instanceName":"1"}),"instanceName":"1"});
            var Q4;
            Q4=makeQuery(id+"F15.opPattern","COPY",BODY,{"derivedFrom":makeQuery(id+"F13.opPattern","COPY",BODY,{"derivedFrom":makeQuery(id+"F1.opExtrude","SWEPT_BODY",BODY,{"disambiguationData":[OSD([sQuery(id+"F0.wireOp",EDGE,"E0"),sQuery(id+"F0.wireOp",EDGE,"E1"),sQuery(id+"F0.wireOp",EDGE,"E2"),sQuery(id+"F0.wireOp",EDGE,"E3"),sQuery(id+"F0.wireOp",EDGE,"E4"),sQuery(id+"F0.wireOp",EDGE,"E5"),sQuery(id+"F0.wireOp",EDGE,"E6"),sQuery(id+"F0.wireOp",EDGE,"E7"),sQuery(id+"F0.wireOp",EDGE,"E8"),sQuery(id+"F0.wireOp",EDGE,"E9"),sQuery(id+"F0.wireOp",EDGE,"E10"),sQuery(id+"F0.wireOp",EDGE,"E11")])]}),"instanceName":"1"}),"instanceName":"1"});
            var Q5;
            Q5=makeQuery(id+"F15.opPattern","COPY",BODY,{"derivedFrom":makeQuery(id+"F14.opPattern","COPY",BODY,{"derivedFrom":makeQuery(id+"F13.opPattern","COPY",BODY,{"derivedFrom":makeQuery(id+"F1.opExtrude","SWEPT_BODY",BODY,{"disambiguationData":[OSD([sQuery(id+"F0.wireOp",EDGE,"E0"),sQuery(id+"F0.wireOp",EDGE,"E1"),sQuery(id+"F0.wireOp",EDGE,"E2"),sQuery(id+"F0.wireOp",EDGE,"E3"),sQuery(id+"F0.wireOp",EDGE,"E4"),sQuery(id+"F0.wireOp",EDGE,"E5"),sQuery(id+"F0.wireOp",EDGE,"E6"),sQuery(id+"F0.wireOp",EDGE,"E7"),sQuery(id+"F0.wireOp",EDGE,"E8"),sQuery(id+"F0.wireOp",EDGE,"E9"),sQuery(id+"F0.wireOp",EDGE,"E10"),sQuery(id+"F0.wireOp",EDGE,"E11")])]}),"instanceName":"1"}),"instanceName":"1"}),"instanceName":"1"});
            var Q6;
            Q6=makeQuery(id+"F14.opPattern","COPY",BODY,{"derivedFrom":makeQuery(id+"F13.opPattern","COPY",BODY,{"derivedFrom":makeQuery(id+"F1.opExtrude","SWEPT_BODY",BODY,{"disambiguationData":[OSD([sQuery(id+"F0.wireOp",EDGE,"E0"),sQuery(id+"F0.wireOp",EDGE,"E1"),sQuery(id+"F0.wireOp",EDGE,"E2"),sQuery(id+"F0.wireOp",EDGE,"E3"),sQuery(id+"F0.wireOp",EDGE,"E4"),sQuery(id+"F0.wireOp",EDGE,"E5"),sQuery(id+"F0.wireOp",EDGE,"E6"),sQuery(id+"F0.wireOp",EDGE,"E7"),sQuery(id+"F0.wireOp",EDGE,"E8"),sQuery(id+"F0.wireOp",EDGE,"E9"),sQuery(id+"F0.wireOp",EDGE,"E10"),sQuery(id+"F0.wireOp",EDGE,"E11")])]}),"instanceName":"1"}),"instanceName":"1"});
            var Q7;
            Q7=makeQuery(id+"F16.opPattern","COPY",FACE,{"derivedFrom":makeQuery(id+"F13.opPattern","COPY",FACE,{"derivedFrom":makeQuery(id+"F1.opExtrude","CAP_FACE",FACE,{"disambiguationData":[OSD([sQuery(id+"F0.wireOp",EDGE,"E0"),sQuery(id+"F0.wireOp",EDGE,"E1"),sQuery(id+"F0.wireOp",EDGE,"E2"),sQuery(id+"F0.wireOp",EDGE,"E3"),sQuery(id+"F0.wireOp",EDGE,"E4"),sQuery(id+"F0.wireOp",EDGE,"E5"),sQuery(id+"F0.wireOp",EDGE,"E6"),sQuery(id+"F0.wireOp",EDGE,"E7"),sQuery(id+"F0.wireOp",EDGE,"E8"),sQuery(id+"F0.wireOp",EDGE,"E9"),sQuery(id+"F0.wireOp",EDGE,"E10"),sQuery(id+"F0.wireOp",EDGE,"E11")])],"isStart":true}),"instanceName":"1"}),"instanceName":"1"});
            mirror(context, id + "F17", {"entities" : qUnion([Q0, Q1, Q2, Q3, Q4, Q5, Q6]), "mirrorPlane" : qUnion([Q7])});
        }
        {
            var Q0;
            Q0=makeQuery(id+"F17.opPattern","COPY",BODY,{"derivedFrom":makeQuery(id+"F14.opPattern","COPY",BODY,{"derivedFrom":makeQuery(id+"F13.opPattern","COPY",BODY,{"derivedFrom":makeQuery(id+"F1.opExtrude","SWEPT_BODY",BODY,{"disambiguationData":[OSD([sQuery(id+"F0.wireOp",EDGE,"E0"),sQuery(id+"F0.wireOp",EDGE,"E1"),sQuery(id+"F0.wireOp",EDGE,"E2"),sQuery(id+"F0.wireOp",EDGE,"E3"),sQuery(id+"F0.wireOp",EDGE,"E4"),sQuery(id+"F0.wireOp",EDGE,"E5"),sQuery(id+"F0.wireOp",EDGE,"E6"),sQuery(id+"F0.wireOp",EDGE,"E7"),sQuery(id+"F0.wireOp",EDGE,"E8"),sQuery(id+"F0.wireOp",EDGE,"E9"),sQuery(id+"F0.wireOp",EDGE,"E10"),sQuery(id+"F0.wireOp",EDGE,"E11")])]}),"instanceName":"1"}),"instanceName":"1"}),"instanceName":"1"});
            var Q1;
            Q1=makeQuery(id+"F17.opPattern","COPY",BODY,{"derivedFrom":makeQuery(id+"F15.opPattern","COPY",BODY,{"derivedFrom":makeQuery(id+"F14.opPattern","COPY",BODY,{"derivedFrom":makeQuery(id+"F13.opPattern","COPY",BODY,{"derivedFrom":makeQuery(id+"F1.opExtrude","SWEPT_BODY",BODY,{"disambiguationData":[OSD([sQuery(id+"F0.wireOp",EDGE,"E0"),sQuery(id+"F0.wireOp",EDGE,"E1"),sQuery(id+"F0.wireOp",EDGE,"E2"),sQuery(id+"F0.wireOp",EDGE,"E3"),sQuery(id+"F0.wireOp",EDGE,"E4"),sQuery(id+"F0.wireOp",EDGE,"E5"),sQuery(id+"F0.wireOp",EDGE,"E6"),sQuery(id+"F0.wireOp",EDGE,"E7"),sQuery(id+"F0.wireOp",EDGE,"E8"),sQuery(id+"F0.wireOp",EDGE,"E9"),sQuery(id+"F0.wireOp",EDGE,"E10"),sQuery(id+"F0.wireOp",EDGE,"E11")])]}),"instanceName":"1"}),"instanceName":"1"}),"instanceName":"1"}),"instanceName":"1"});
            var Q2;
            Q2=makeQuery(id+"F17.opPattern","COPY",FACE,{"derivedFrom":makeQuery(id+"F14.opPattern","COPY",FACE,{"derivedFrom":makeQuery(id+"F13.opPattern","COPY",FACE,{"derivedFrom":makeQuery(id+"F1.opExtrude","CAP_FACE",FACE,{"disambiguationData":[OSD([sQuery(id+"F0.wireOp",EDGE,"E0"),sQuery(id+"F0.wireOp",EDGE,"E1"),sQuery(id+"F0.wireOp",EDGE,"E2"),sQuery(id+"F0.wireOp",EDGE,"E3"),sQuery(id+"F0.wireOp",EDGE,"E4"),sQuery(id+"F0.wireOp",EDGE,"E5"),sQuery(id+"F0.wireOp",EDGE,"E6"),sQuery(id+"F0.wireOp",EDGE,"E7"),sQuery(id+"F0.wireOp",EDGE,"E8"),sQuery(id+"F0.wireOp",EDGE,"E9"),sQuery(id+"F0.wireOp",EDGE,"E10"),sQuery(id+"F0.wireOp",EDGE,"E11")])],"isStart":false}),"instanceName":"1"}),"instanceName":"1"}),"instanceName":"1"});
            mirror(context, id + "F18", {"entities" : qUnion([Q0, Q1]), "mirrorPlane" : qUnion([Q2])});
        }
        {
            var Q0;
            Q0=makeQuery(id+"F18.opPattern","COPY",BODY,{"derivedFrom":makeQuery(id+"F17.opPattern","COPY",BODY,{"derivedFrom":makeQuery(id+"F15.opPattern","COPY",BODY,{"derivedFrom":makeQuery(id+"F14.opPattern","COPY",BODY,{"derivedFrom":makeQuery(id+"F13.opPattern","COPY",BODY,{"derivedFrom":makeQuery(id+"F1.opExtrude","SWEPT_BODY",BODY,{"disambiguationData":[OSD([sQuery(id+"F0.wireOp",EDGE,"E0"),sQuery(id+"F0.wireOp",EDGE,"E1"),sQuery(id+"F0.wireOp",EDGE,"E2"),sQuery(id+"F0.wireOp",EDGE,"E3"),sQuery(id+"F0.wireOp",EDGE,"E4"),sQuery(id+"F0.wireOp",EDGE,"E5"),sQuery(id+"F0.wireOp",EDGE,"E6"),sQuery(id+"F0.wireOp",EDGE,"E7"),sQuery(id+"F0.wireOp",EDGE,"E8"),sQuery(id+"F0.wireOp",EDGE,"E9"),sQuery(id+"F0.wireOp",EDGE,"E10"),sQuery(id+"F0.wireOp",EDGE,"E11")])]}),"instanceName":"1"}),"instanceName":"1"}),"instanceName":"1"}),"instanceName":"1"}),"instanceName":"1"});
            var Q1;
            Q1=makeQuery(id+"F18.opPattern","COPY",FACE,{"derivedFrom":makeQuery(id+"F17.opPattern","COPY",FACE,{"derivedFrom":makeQuery(id+"F15.opPattern","COPY",FACE,{"derivedFrom":makeQuery(id+"F14.opPattern","COPY",FACE,{"derivedFrom":makeQuery(id+"F13.opPattern","COPY",FACE,{"derivedFrom":makeQuery(id+"F1.opExtrude","CAP_FACE",FACE,{"disambiguationData":[OSD([sQuery(id+"F0.wireOp",EDGE,"E0"),sQuery(id+"F0.wireOp",EDGE,"E1"),sQuery(id+"F0.wireOp",EDGE,"E2"),sQuery(id+"F0.wireOp",EDGE,"E3"),sQuery(id+"F0.wireOp",EDGE,"E4"),sQuery(id+"F0.wireOp",EDGE,"E5"),sQuery(id+"F0.wireOp",EDGE,"E6"),sQuery(id+"F0.wireOp",EDGE,"E7"),sQuery(id+"F0.wireOp",EDGE,"E8"),sQuery(id+"F0.wireOp",EDGE,"E9"),sQuery(id+"F0.wireOp",EDGE,"E10"),sQuery(id+"F0.wireOp",EDGE,"E11")])],"isStart":false}),"instanceName":"1"}),"instanceName":"1"}),"instanceName":"1"}),"instanceName":"1"}),"instanceName":"1"});
            mirror(context, id + "F19", {"entities" : qUnion([Q0]), "mirrorPlane" : qUnion([Q1])});
        }
        {
            var Q0;
            Q0=makeQuery(id+"F19.opPattern","COPY",FACE,{"derivedFrom":makeQuery(id+"F18.opPattern","COPY",FACE,{"derivedFrom":makeQuery(id+"F17.opPattern","COPY",FACE,{"derivedFrom":makeQuery(id+"F15.opPattern","COPY",FACE,{"derivedFrom":makeQuery(id+"F14.opPattern","COPY",FACE,{"derivedFrom":makeQuery(id+"F13.opPattern","COPY",FACE,{"derivedFrom":makeQuery(id+"F1.opExtrude","CAP_FACE",FACE,{"disambiguationData":[OSD([sQuery(id+"F0.wireOp",EDGE,"E0"),sQuery(id+"F0.wireOp",EDGE,"E1"),sQuery(id+"F0.wireOp",EDGE,"E2"),sQuery(id+"F0.wireOp",EDGE,"E3"),sQuery(id+"F0.wireOp",EDGE,"E4"),sQuery(id+"F0.wireOp",EDGE,"E5"),sQuery(id+"F0.wireOp",EDGE,"E6"),sQuery(id+"F0.wireOp",EDGE,"E7"),sQuery(id+"F0.wireOp",EDGE,"E8"),sQuery(id+"F0.wireOp",EDGE,"E9"),sQuery(id+"F0.wireOp",EDGE,"E10"),sQuery(id+"F0.wireOp",EDGE,"E11")])],"isStart":true}),"instanceName":"1"}),"instanceName":"1"}),"instanceName":"1"}),"instanceName":"1"}),"instanceName":"1"}),"instanceName":"1"});
            var sketch = newSketch(context, id + "F20", { "sketchPlane" : qUnion([Q0])});
            skLineSegment(sketch, "E97", {"start": v(71.25, -171) * mm, "end": v(51.07, 0) * mm});
            skLineSegment(sketch, "E98", {"start": v(51.07, 0) * mm, "end": v(71.25, 171) * mm});
            skLineSegment(sketch, "E99", {"start": v(71.25, 171) * mm, "end": v(-71.25, 171) * mm});
            skLineSegment(sketch, "E100", {"start": v(-71.25, 171) * mm, "end": v(-51.07, 0) * mm});
            skLineSegment(sketch, "E101", {"start": v(-51.07, 0) * mm, "end": v(-71.25, -171) * mm});
            skLineSegment(sketch, "E102", {"start": v(-71.25, -171) * mm, "end": v(71.25, -171) * mm});
            skSolve(sketch);
        }
        {
            var Q0;
            Q0 = qSketchRegion(id + "F20", true);
            extrude(context, id + "F21", {"entities" : qUnion([Q0]), "depth" : 4 * mm});
        }
    });
